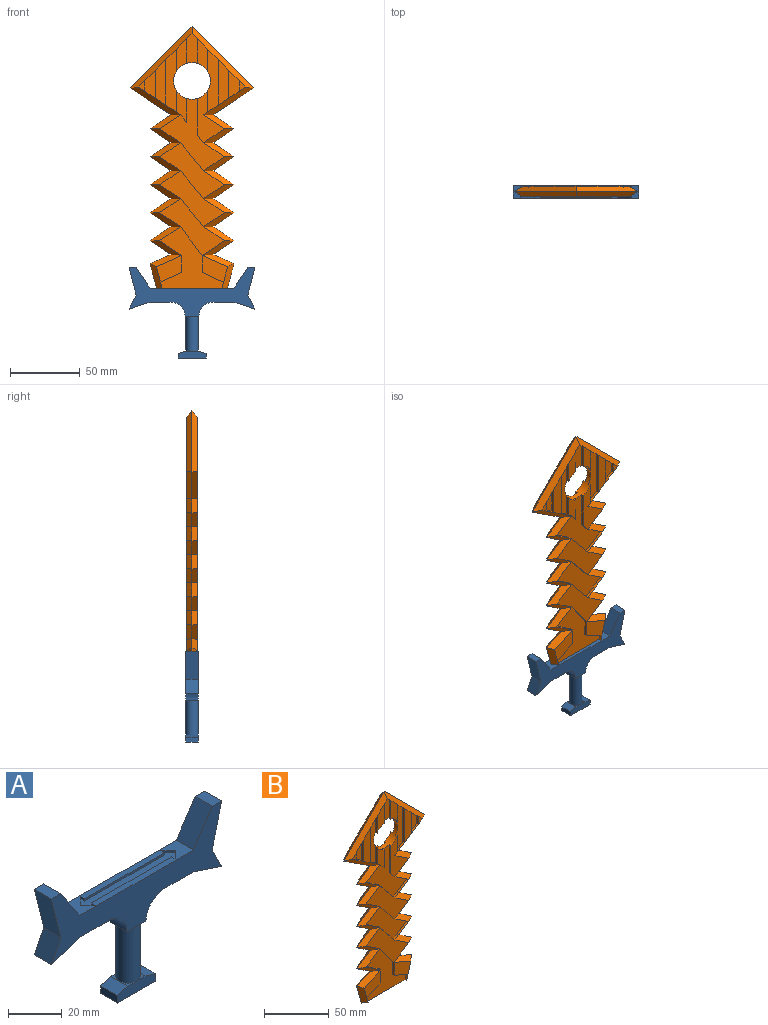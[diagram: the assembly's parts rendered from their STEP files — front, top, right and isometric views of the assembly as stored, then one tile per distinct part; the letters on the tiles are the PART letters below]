
ASSEMBLY  parts=2 mates=1
PART A: 40 faces, bbox 90x9x65 mm
  f0: plane 9x4.51mm, normal (0,0,1), area 8.8mm2, adj f32,f34,f36,f38
  f1: plane 9x3.33mm, normal (1,0,0), area 30mm2, adj f34,f36,f37,f38
  f2: plane 9x5mm, normal (0,0,-1), area 13.2mm2, adj f16,f17,f30,f32
  f3: plane 15x9mm, normal (0,0,-1), area 135mm2, adj f5,f16,f17,f31
  f4: plane 15x9mm, normal (0,0,-1), area 135mm2, adj f15,f16,f17,f30
  f5: plane 15x9mm, normal (-0.32,0,-0.95), area 142.3mm2, adj f3,f6,f16,f17
  f6: plane 10x9mm, normal (0.89,0,0.45), area 100.6mm2, adj f5,f7,f16,f17
  f7: plane 20x9mm, normal (0.97,0,-0.24), area 185.5mm2, adj f6,f8,f16,f17
  f8: plane 9x5mm, normal (0,0,1), area 45mm2, adj f7,f9,f16,f17
  f9: plane 15x10mm, normal (-0.83,0,0.55), area 162.2mm2, adj f8,f10,f16,f17
  f10: plane 60x9mm, normal (0,0,1), area 352.5mm2, adj f9,f11,f16,f17,f18,f19,f20,f21
  f11: plane 15x10mm, normal (0.83,0,0.55), area 162.2mm2, adj f10,f12,f16,f17
  f12: plane 9x5mm, normal (0,0,1), area 45mm2, adj f11,f13,f16,f17
  f13: plane 20x9mm, normal (-0.97,0,-0.24), area 185.5mm2, adj f12,f14,f16,f17
  f14: plane 10x9mm, normal (-0.89,0,0.45), area 100.6mm2, adj f13,f15,f16,f17
  f15: plane 15x9mm, normal (0.32,0,-0.95), area 142.3mm2, adj f4,f14,f16,f17
  f16: plane 90x35mm, normal (0,-1,0), area 1267.9mm2, adj f2,f3,f4,f5,f6,f7,f8,f9
  f17: plane 90x35mm, normal (0,1,0), area 1267.9mm2, adj f2,f3,f4,f5,f6,f7,f8,f9
  f18: plane 3.89x3.75mm, normal (-0.69,0.72,0), area 5.4mm2, adj f10,f19,f27,f28
  f19: plane 3.89x3.75mm, normal (-0.69,-0.72,0), area 5.4mm2, adj f10,f18,f20,f28
  f20: plane 1.88x1mm, normal (1,0,0), area 1.9mm2, adj f10,f19,f21,f28
  f21: plane 42.22x1mm, normal (0,-1,0), area 42.2mm2, adj f10,f20,f22,f28
  f22: plane 1.88x1mm, normal (-1,0,0), area 1.9mm2, adj f10,f21,f23,f28
  f23: plane 3.89x3.75mm, normal (0.69,-0.72,0), area 5.4mm2, adj f10,f22,f24,f28
  f24: plane 3.89x3.75mm, normal (0.69,0.72,0), area 5.4mm2, adj f10,f23,f25,f28
  f25: plane 1.88x1mm, normal (-1,0,0), area 1.9mm2, adj f10,f24,f26,f28
  f26: plane 42.22x1mm, normal (0,1,0), area 42.2mm2, adj f10,f25,f27,f28
  f27: plane 1.88x1mm, normal (1,0,0), area 1.9mm2, adj f10,f18,f26,f28
  f28: plane 50x7.5mm, normal (0,0,1), area 187.5mm2, adj f18,f19,f20,f21,f22,f23,f24,f25
  f29: plane 9x5mm, normal (0,0,-1), area 13.2mm2, adj f16,f17,f31,f32
  f30: cylinder r=10mm len=10mm, axis (0,1,0), area 141.4mm2, adj f2,f4,f16,f17
  f31: cylinder r=10mm len=10mm, axis (0,-1,0), area 141.4mm2, adj f3,f16,f17,f29
  f32: cylinder r=4.5mm len=25mm, axis (0,0,1), area 706.9mm2, adj f0,f2,f29,f33
  f33: plane 9x4.54mm, normal (0,0,1), area 9.1mm2, adj f32,f34,f36,f39
  f34: plane 20.08x5mm, normal (0,-1,0), area 91.2mm2, adj f0,f1,f33,f35,f37,f38,f39
  f35: plane 9x3.33mm, normal (-1,0,0), area 30mm2, adj f34,f36,f37,f39
  f36: plane 20.08x5mm, normal (0,1,0), area 91.2mm2, adj f0,f1,f33,f35,f37,f38,f39
  f37: plane 20.08x9mm, normal (0,0,-1), area 180.7mm2, adj f1,f34,f35,f36
  f38: plane 9x5.57mm, normal (0.29,0,0.96), area 52.3mm2, adj f0,f1,f34,f36
  f39: plane 9x5.46mm, normal (-0.29,0,0.96), area 51.4mm2, adj f33,f34,f35,f36
PART B: 190 faces, bbox 88.6x7.5x188.6 mm
  f0: plane 50x7.5mm, normal (0,0,-1), area 187.3mm2, adj f26,f27,f80,f81,f112,f113,f118,f166
  f1: cylinder r=13.13mm len=26.26mm, axis (0,1,0), area 454.8mm2, adj f3,f5,f6,f10,f15,f17,f18,f20
  f2: plane 32.54x7.5mm, normal (0,-1,0), area 197.4mm2, adj f50,f52,f157,f187
  f3: plane 23.46x7.5mm, normal (0,-1,0), area 120.3mm2, adj f1,f52,f138,f159
  f4: plane 7.67x4.62mm, normal (0,-1,0), area 17.7mm2, adj f50,f52,f185
  f5: plane 22.92x7.5mm, normal (0,-1,0), area 112.8mm2, adj f1,f56,f143,f144,f154
  f6: plane 23.46x7.5mm, normal (0,-1,0), area 120.3mm2, adj f1,f54,f137,f155
  f7: plane 32.54x7.5mm, normal (0,-1,0), area 197.4mm2, adj f54,f56,f152,f183
  f8: plane 19.19x18.33mm, normal (0,-1,0), area 207.5mm2, adj f26,f28,f168,f169
  f9: plane 46.48x40.69mm, normal (0,-1,0), area 645.5mm2, adj f30,f32,f70,f72,f170,f174
  f10: plane 37.51x19.49mm, normal (0,-1,0), area 328.3mm2, adj f1,f46,f48,f50,f141,f142,f160
  f11: plane 46.48x40mm, normal (0,-1,0), area 629.6mm2, adj f38,f40,f62,f64,f147,f177
  f12: plane 18.94x18.33mm, normal (0,-1,0), area 205.4mm2, adj f78,f80,f164,f165
  f13: plane 7.67x4.62mm, normal (0,-1,0), area 17.7mm2, adj f54,f56,f181
  f14: plane 32.54x7.5mm, normal (0,1,0), area 197.4mm2, adj f55,f57,f103,f133
  f15: plane 23.46x7.5mm, normal (0,1,0), area 120.3mm2, adj f1,f55,f84,f105
  f16: plane 7.67x4.62mm, normal (0,1,0), area 17.7mm2, adj f55,f57,f131
  f17: plane 22.92x7.5mm, normal (0,1,0), area 112.8mm2, adj f1,f51,f89,f90,f100
  f18: plane 23.46x7.5mm, normal (0,1,0), area 120.3mm2, adj f1,f53,f83,f101
  f19: plane 32.54x7.5mm, normal (0,1,0), area 197.4mm2, adj f51,f53,f98,f129
  f20: plane 37.51x19.49mm, normal (0,1,0), area 328.3mm2, adj f1,f57,f59,f61,f87,f88,f106
  f21: plane 46.48x40mm, normal (0,1,0), area 629.6mm2, adj f43,f45,f67,f69,f93,f122
  f22: plane 18.88x18.33mm, normal (0,1,0), area 204.9mm2, adj f27,f29,f110,f111
  f23: plane 18.88x18.33mm, normal (0,1,0), area 204.9mm2, adj f79,f81,f114,f115
  f24: plane 46.48x40.69mm, normal (0,1,0), area 645.5mm2, adj f35,f37,f75,f77,f116,f119
  f25: plane 7.67x4.62mm, normal (0,1,0), area 17.7mm2, adj f51,f53,f127
  f26: plane 18.44x8.89mm, normal (0.68,-0.71,-0.19), area 95.5mm2, adj f0,f8,f27,f28,f167
  f27: plane 18.44x8.89mm, normal (0.68,0.71,-0.19), area 95.5mm2, adj f0,f22,f26,f29,f112
  f28: plane 22.79x8.7mm, normal (0.28,-0.71,0.65), area 96.4mm2, adj f8,f26,f29,f30
  f29: plane 22.79x8.7mm, normal (0.28,0.71,0.65), area 96.4mm2, adj f22,f27,f28,f31
  f30: plane 22.79x10.69mm, normal (0.39,-0.71,-0.59), area 98.9mm2, adj f9,f28,f31,f32
  f31: plane 22.79x10.69mm, normal (0.39,0.71,-0.59), area 98.9mm2, adj f29,f30,f33,f109
  f32: plane 21.76x10mm, normal (0.39,-0.71,0.59), area 95.6mm2, adj f9,f30,f33,f34
  f33: plane 21.76x10mm, normal (0.39,0.71,0.59), area 95.6mm2, adj f31,f32,f35,f117
  f34: plane 21.76x10mm, normal (0.39,-0.71,-0.59), area 95.6mm2, adj f32,f35,f36,f175
  f35: plane 21.76x10mm, normal (0.39,0.71,-0.59), area 95.6mm2, adj f24,f33,f34,f37
  f36: plane 21.76x10mm, normal (0.39,-0.71,0.59), area 95.6mm2, adj f34,f37,f38,f176
  f37: plane 21.76x10mm, normal (0.39,0.71,0.59), area 95.6mm2, adj f24,f35,f36,f39
  f38: plane 21.76x10mm, normal (0.39,-0.71,-0.59), area 95.6mm2, adj f11,f36,f39,f40
  f39: plane 21.76x10mm, normal (0.39,0.71,-0.59), area 95.6mm2, adj f37,f38,f41,f124
  f40: plane 21.76x10mm, normal (0.39,-0.71,0.59), area 95.6mm2, adj f11,f38,f41,f42
  f41: plane 21.76x10mm, normal (0.39,0.71,0.59), area 95.6mm2, adj f39,f40,f43,f123
  f42: plane 21.76x10mm, normal (0.39,-0.71,-0.59), area 95.6mm2, adj f40,f43,f44,f148
  f43: plane 21.76x10mm, normal (0.39,0.71,-0.59), area 95.6mm2, adj f21,f41,f42,f45
  f44: plane 21.76x10mm, normal (0.39,-0.71,0.59), area 95.6mm2, adj f42,f45,f46,f149
  f45: plane 21.76x10mm, normal (0.39,0.71,0.59), area 95.6mm2, adj f21,f43,f44,f47
  f46: plane 21.76x10mm, normal (0.39,-0.71,-0.59), area 95.6mm2, adj f10,f44,f47,f48
  f47: plane 21.76x10mm, normal (0.39,0.71,-0.59), area 95.6mm2, adj f45,f46,f49,f92
  f48: plane 21.79x10.02mm, normal (0.39,-0.71,0.59), area 95.7mm2, adj f10,f46,f49,f50
  f49: plane 21.79x10.02mm, normal (0.39,0.71,0.59), area 95.7mm2, adj f47,f48,f51,f91
  f50: plane 36.07x19.88mm, normal (0.39,-0.71,-0.59), area 188.7mm2, adj f2,f4,f10,f48,f51,f52,f161,f188
  f51: plane 36.07x19.88mm, normal (0.39,0.71,-0.59), area 188.7mm2, adj f17,f19,f25,f49,f50,f53,f99,f128
  f52: plane 44.28x44.28mm, normal (0.5,-0.71,0.5), area 309.9mm2, adj f2,f3,f4,f50,f53,f54,f139,f158
  f53: plane 44.28x44.28mm, normal (0.5,0.71,0.5), area 309.9mm2, adj f18,f19,f25,f51,f52,f55,f82,f97
  f54: plane 44.28x44.28mm, normal (-0.5,-0.71,0.5), area 309.9mm2, adj f6,f7,f13,f52,f55,f56,f136,f151
  f55: plane 44.28x44.28mm, normal (-0.5,0.71,0.5), area 309.9mm2, adj f14,f15,f16,f53,f54,f57,f85,f104
  f56: plane 36.07x19.88mm, normal (-0.39,-0.71,-0.59), area 188.7mm2, adj f5,f7,f13,f54,f57,f58,f153,f182
  f57: plane 36.07x19.88mm, normal (-0.39,0.71,-0.59), area 188.7mm2, adj f14,f16,f20,f55,f56,f59,f107,f134
  f58: plane 21.79x10.02mm, normal (-0.39,-0.71,0.59), area 95.7mm2, adj f56,f59,f60,f145
  f59: plane 21.79x10.02mm, normal (-0.39,0.71,0.59), area 95.7mm2, adj f20,f57,f58,f61
  f60: plane 21.76x10mm, normal (-0.39,-0.71,-0.59), area 95.6mm2, adj f58,f61,f62,f146
  f61: plane 21.76x10mm, normal (-0.39,0.71,-0.59), area 95.6mm2, adj f20,f59,f60,f63
  f62: plane 21.76x10mm, normal (-0.39,-0.71,0.59), area 95.6mm2, adj f11,f60,f63,f64
  f63: plane 21.76x10mm, normal (-0.39,0.71,0.59), area 95.6mm2, adj f61,f62,f65,f95
  f64: plane 21.76x10mm, normal (-0.39,-0.71,-0.59), area 95.6mm2, adj f11,f62,f65,f66
  f65: plane 21.76x10mm, normal (-0.39,0.71,-0.59), area 95.6mm2, adj f63,f64,f67,f94
  f66: plane 21.76x10mm, normal (-0.39,-0.71,0.59), area 95.6mm2, adj f64,f67,f68,f178
  f67: plane 21.76x10mm, normal (-0.39,0.71,0.59), area 95.6mm2, adj f21,f65,f66,f69
  f68: plane 21.76x10mm, normal (-0.39,-0.71,-0.59), area 95.6mm2, adj f66,f69,f70,f173
  f69: plane 21.76x10mm, normal (-0.39,0.71,-0.59), area 95.6mm2, adj f21,f67,f68,f71
  f70: plane 21.76x10mm, normal (-0.39,-0.71,0.59), area 95.6mm2, adj f9,f68,f71,f72
  f71: plane 21.76x10mm, normal (-0.39,0.71,0.59), area 95.6mm2, adj f69,f70,f73,f121
  f72: plane 21.76x10mm, normal (-0.39,-0.71,-0.59), area 95.6mm2, adj f9,f70,f73,f74
  f73: plane 21.76x10mm, normal (-0.39,0.71,-0.59), area 95.6mm2, adj f71,f72,f75,f120
  f74: plane 21.76x10mm, normal (-0.39,-0.71,0.59), area 95.6mm2, adj f72,f75,f76,f171
  f75: plane 21.76x10mm, normal (-0.39,0.71,0.59), area 95.6mm2, adj f24,f73,f74,f77
  f76: plane 22.79x10.69mm, normal (-0.39,-0.71,-0.59), area 98.9mm2, adj f74,f77,f78,f163
  f77: plane 22.79x10.69mm, normal (-0.39,0.71,-0.59), area 98.9mm2, adj f24,f75,f76,f79
  f78: plane 22.79x8.7mm, normal (-0.28,-0.71,0.65), area 96.4mm2, adj f12,f76,f79,f80
  f79: plane 22.79x8.7mm, normal (-0.28,0.71,0.65), area 96.4mm2, adj f23,f77,f78,f81
  f80: plane 18.44x8.89mm, normal (-0.68,-0.71,-0.19), area 95.5mm2, adj f0,f12,f78,f81,f166
  f81: plane 18.44x8.89mm, normal (-0.68,0.71,-0.19), area 95.5mm2, adj f0,f23,f79,f80,f113
  f82: plane 3.75x3.75mm, normal (-0.71,0,-0.71), area 10mm2, adj f53,f83,f85,f86
  f83: plane 17.64x1.88mm, normal (-1,0,0), area 33.2mm2, adj f1,f18,f82,f86
  f84: plane 17.64x1.88mm, normal (1,0,0), area 33.2mm2, adj f1,f15,f85,f86
  f85: plane 3.75x3.75mm, normal (0.71,0,-0.71), area 10mm2, adj f55,f82,f84,f86
  f86: plane 21.39x7.5mm, normal (0,1,0), area 143.6mm2, adj f1,f82,f83,f84,f85
  f87: plane 5.46x4.49mm, normal (0.77,0,-0.63), area 13.3mm2, adj f20,f88,f95,f96
  f88: plane 26.23x1.88mm, normal (1,0,0), area 49.3mm2, adj f1,f20,f87,f96
  f89: plane 17.11x1.88mm, normal (-1,0,0), area 32.2mm2, adj f1,f17,f90,f96
  f90: plane 5.43x4.46mm, normal (0.77,0,-0.63), area 13.2mm2, adj f17,f89,f91,f96
  f91: plane 15.03x10.02mm, normal (-0.55,0,-0.83), area 34mm2, adj f49,f90,f92,f96
  f92: plane 15x10mm, normal (-0.55,0,0.83), area 33.9mm2, adj f47,f91,f93,f96
  f93: plane 20x16.48mm, normal (-0.77,0,0.64), area 48.7mm2, adj f21,f92,f94,f96
  f94: plane 15x10mm, normal (0.55,0,0.83), area 33.9mm2, adj f65,f93,f95,f96
  f95: plane 15x10mm, normal (0.55,0,-0.83), area 33.9mm2, adj f63,f87,f94,f96
  f96: plane 51.7x46.48mm, normal (0,1,0), area 789.8mm2, adj f1,f87,f88,f89,f90,f91,f92,f93
  f97: plane 7.5x7.5mm, normal (-0.71,0,-0.71), area 19.9mm2, adj f53,f98,f101,f102
  f98: plane 32.54x1.88mm, normal (-1,0,0), area 61.2mm2, adj f19,f97,f99,f102
  f99: plane 7.5x4.94mm, normal (-0.55,0,0.84), area 16.9mm2, adj f51,f98,f100,f102
  f100: plane 15.49x1.88mm, normal (1,0,0), area 29.1mm2, adj f1,f17,f99,f102
  f101: plane 15.96x1.88mm, normal (1,0,0), area 30mm2, adj f1,f18,f97,f102
  f102: plane 44.98x7.5mm, normal (0,1,0), area 273.5mm2, adj f1,f97,f98,f99,f100,f101
  f103: plane 32.54x1.88mm, normal (1,0,0), area 61.2mm2, adj f14,f104,f107,f108
  f104: plane 7.5x7.5mm, normal (0.71,0,-0.71), area 19.9mm2, adj f55,f103,f105,f108
  f105: plane 15.96x1.88mm, normal (-1,0,0), area 30mm2, adj f1,f15,f104,f108
  f106: plane 15.49x1.88mm, normal (-1,0,0), area 29.1mm2, adj f1,f20,f107,f108
  f107: plane 7.5x4.94mm, normal (0.55,0,0.84), area 16.9mm2, adj f57,f103,f106,f108
  f108: plane 44.98x7.5mm, normal (0,1,0), area 273.5mm2, adj f1,f103,f104,f105,f106,f107
  f109: plane 16.03x10.69mm, normal (-0.55,0,0.83), area 36.2mm2, adj f31,f110,f117,f118
  f110: plane 12.16x1.88mm, normal (-1,0,0), area 22.9mm2, adj f22,f109,f111,f118
  f111: plane 15.38x6.72mm, normal (-0.4,0,-0.92), area 31.6mm2, adj f22,f110,f112,f118
  f112: plane 5.43x1.88mm, normal (-0.97,0,0.26), area 10.6mm2, adj f0,f27,f111,f118
  f113: plane 5.43x1.88mm, normal (0.97,0,0.26), area 10.6mm2, adj f0,f81,f114,f118
  f114: plane 15.38x6.72mm, normal (0.4,0,-0.92), area 31.6mm2, adj f23,f113,f115,f118
  f115: plane 12.16x1.88mm, normal (1,0,0), area 22.9mm2, adj f23,f114,f116,f118
  f116: plane 20.69x15.45mm, normal (0.8,0,-0.6), area 48.5mm2, adj f24,f115,f117,f118
  f117: plane 15x10mm, normal (-0.55,0,-0.83), area 33.9mm2, adj f33,f109,f116,f118
  f118: plane 45.83x45mm, normal (0,1,0), area 922.5mm2, adj f0,f109,f110,f111,f112,f113,f114,f115
  f119: plane 20x16.48mm, normal (-0.77,0,0.64), area 48.7mm2, adj f24,f120,f124,f125
  f120: plane 15x10mm, normal (0.55,0,0.83), area 33.9mm2, adj f73,f119,f121,f125
  f121: plane 15x10mm, normal (0.55,0,-0.83), area 33.9mm2, adj f71,f120,f122,f125
  f122: plane 20x16.48mm, normal (0.77,0,-0.64), area 48.7mm2, adj f21,f121,f123,f125
  f123: plane 15x10mm, normal (-0.55,0,-0.83), area 33.9mm2, adj f41,f122,f124,f125
  f124: plane 15x10mm, normal (-0.55,0,0.83), area 33.9mm2, adj f39,f119,f123,f125
  f125: plane 46.48x40mm, normal (0,1,0), area 629.6mm2, adj f119,f120,f121,f122,f123,f124
  f126: plane 7.5x7.5mm, normal (-0.71,0,-0.71), area 19.9mm2, adj f53,f127,f129,f130
  f127: plane 7.67x1.88mm, normal (-1,0,0), area 14.4mm2, adj f25,f126,f128,f130
  f128: plane 7.5x4.94mm, normal (-0.55,0,0.84), area 16.9mm2, adj f51,f127,f129,f130
  f129: plane 20.1x1.88mm, normal (1,0,0), area 37.8mm2, adj f19,f126,f128,f130
  f130: plane 20.1x7.5mm, normal (0,1,0), area 104.1mm2, adj f126,f127,f128,f129
  f131: plane 7.67x1.88mm, normal (1,0,0), area 14.4mm2, adj f16,f132,f134,f135
  f132: plane 7.5x7.5mm, normal (0.71,0,-0.71), area 19.9mm2, adj f55,f131,f133,f135
  f133: plane 20.1x1.88mm, normal (-1,0,0), area 37.8mm2, adj f14,f132,f134,f135
  f134: plane 7.5x4.94mm, normal (0.55,0,0.84), area 16.9mm2, adj f57,f131,f133,f135
  f135: plane 20.1x7.5mm, normal (0,1,0), area 104.1mm2, adj f131,f132,f133,f134
  f136: plane 3.75x3.75mm, normal (0.71,0,-0.71), area 9.9mm2, adj f54,f137,f139,f140
  f137: plane 17.64x1.88mm, normal (1,0,0), area 33.1mm2, adj f1,f6,f136,f140
  f138: plane 17.64x1.88mm, normal (-1,0,0), area 33.1mm2, adj f1,f3,f139,f140
  f139: plane 3.75x3.75mm, normal (-0.71,0,-0.71), area 9.9mm2, adj f52,f136,f138,f140
  f140: plane 21.39x7.5mm, normal (0,-1,0), area 143.6mm2, adj f1,f136,f137,f138,f139
  f141: plane 5.46x4.49mm, normal (-0.77,0,-0.63), area 13.3mm2, adj f10,f142,f149,f150
  f142: plane 26.23x1.88mm, normal (-1,0,0), area 49.2mm2, adj f1,f10,f141,f150
  f143: plane 17.11x1.88mm, normal (1,0,0), area 32.1mm2, adj f1,f5,f144,f150
  f144: plane 5.43x4.46mm, normal (-0.77,0,-0.63), area 13.2mm2, adj f5,f143,f145,f150
  f145: plane 15.03x10.02mm, normal (0.55,0,-0.83), area 33.9mm2, adj f58,f144,f146,f150
  f146: plane 15x10mm, normal (0.55,0,0.83), area 33.8mm2, adj f60,f145,f147,f150
  f147: plane 20x16.48mm, normal (0.77,0,0.64), area 48.6mm2, adj f11,f146,f148,f150
  f148: plane 15x10mm, normal (-0.55,0,0.83), area 33.8mm2, adj f42,f147,f149,f150
  f149: plane 15x10mm, normal (-0.55,0,-0.83), area 33.8mm2, adj f44,f141,f148,f150
  f150: plane 51.7x46.48mm, normal (0,-1,0), area 789.8mm2, adj f1,f141,f142,f143,f144,f145,f146,f147
  f151: plane 7.5x7.5mm, normal (0.71,0,-0.71), area 19.9mm2, adj f54,f152,f155,f156
  f152: plane 32.54x1.88mm, normal (1,0,0), area 61mm2, adj f7,f151,f153,f156
  f153: plane 7.5x4.94mm, normal (0.55,0,0.84), area 16.8mm2, adj f56,f152,f154,f156
  f154: plane 15.49x1.88mm, normal (-1,0,0), area 29mm2, adj f1,f5,f153,f156
  f155: plane 15.96x1.88mm, normal (-1,0,0), area 29.9mm2, adj f1,f6,f151,f156
  f156: plane 44.98x7.5mm, normal (0,-1,0), area 273.5mm2, adj f1,f151,f152,f153,f154,f155
  f157: plane 32.54x1.88mm, normal (-1,0,0), area 61mm2, adj f2,f158,f161,f162
  f158: plane 7.5x7.5mm, normal (-0.71,0,-0.71), area 19.9mm2, adj f52,f157,f159,f162
  f159: plane 15.96x1.88mm, normal (1,0,0), area 29.9mm2, adj f1,f3,f158,f162
  f160: plane 15.49x1.88mm, normal (1,0,0), area 29mm2, adj f1,f10,f161,f162
  f161: plane 7.5x4.94mm, normal (-0.55,0,0.84), area 16.8mm2, adj f50,f157,f160,f162
  f162: plane 44.98x7.5mm, normal (0,-1,0), area 273.5mm2, adj f1,f157,f158,f159,f160,f161
  f163: plane 16.03x10.69mm, normal (0.55,0,0.83), area 36.1mm2, adj f76,f164,f171,f172
  f164: plane 12.16x1.88mm, normal (1,0,0), area 22.8mm2, adj f12,f163,f165,f172
  f165: plane 15.36x6.79mm, normal (0.4,0,-0.91), area 31.5mm2, adj f12,f164,f166,f172
  f166: plane 5.37x1.88mm, normal (0.97,0,0.26), area 10.4mm2, adj f0,f80,f165,f172
  f167: plane 5.12x1.88mm, normal (-0.97,0,0.26), area 10mm2, adj f0,f26,f168,f172
  f168: plane 15.29x7.03mm, normal (-0.42,0,-0.91), area 31.6mm2, adj f8,f167,f169,f172
  f169: plane 12.16x1.88mm, normal (-1,0,0), area 22.8mm2, adj f8,f168,f170,f172
  f170: plane 20.69x15.45mm, normal (-0.8,0,-0.6), area 48.4mm2, adj f9,f169,f171,f172
  f171: plane 15x10mm, normal (0.55,0,-0.83), area 33.8mm2, adj f74,f163,f170,f172
  f172: plane 45.74x45mm, normal (0,-1,0), area 919.3mm2, adj f0,f163,f164,f165,f166,f167,f168,f169
  f173: plane 15x10mm, normal (0.55,0,0.83), area 33.8mm2, adj f68,f174,f178,f179
  f174: plane 20x16.48mm, normal (0.77,0,0.64), area 48.6mm2, adj f9,f173,f175,f179
  f175: plane 15x10mm, normal (-0.55,0,0.83), area 33.8mm2, adj f34,f174,f176,f179
  f176: plane 15x10mm, normal (-0.55,0,-0.83), area 33.8mm2, adj f36,f175,f177,f179
  f177: plane 20x16.48mm, normal (-0.77,0,-0.64), area 48.6mm2, adj f11,f176,f178,f179
  f178: plane 15x10mm, normal (0.55,0,-0.83), area 33.8mm2, adj f66,f173,f177,f179
  f179: plane 46.48x40mm, normal (0,-1,0), area 629.6mm2, adj f173,f174,f175,f176,f177,f178
  f180: plane 7.5x7.5mm, normal (0.71,0,-0.71), area 19.9mm2, adj f54,f181,f183,f184
  f181: plane 7.67x1.88mm, normal (1,0,0), area 14.4mm2, adj f13,f180,f182,f184
  f182: plane 7.5x4.94mm, normal (0.55,0,0.84), area 16.8mm2, adj f56,f181,f183,f184
  f183: plane 20.1x1.88mm, normal (-1,0,0), area 37.7mm2, adj f7,f180,f182,f184
  f184: plane 20.1x7.5mm, normal (0,-1,0), area 104.1mm2, adj f180,f181,f182,f183
  f185: plane 7.67x1.88mm, normal (-1,0,0), area 14.4mm2, adj f4,f186,f188,f189
  f186: plane 7.5x7.5mm, normal (-0.71,0,-0.71), area 19.9mm2, adj f52,f185,f187,f189
  f187: plane 20.1x1.88mm, normal (1,0,0), area 37.7mm2, adj f2,f186,f188,f189
  f188: plane 7.5x4.94mm, normal (-0.55,0,0.84), area 16.8mm2, adj f50,f185,f187,f189
  f189: plane 20.1x7.5mm, normal (0,-1,0), area 104.1mm2, adj f185,f186,f187,f188
PLACE A t=(-32.45,-27.8,-6.57)mm
PLACE B t=(-32.45,-28.55,46.16)mm
MATE fastened B.f0 <-> A.f32  axis (0,0,-1) through (-32.45,-32.3,-3.84)mm
